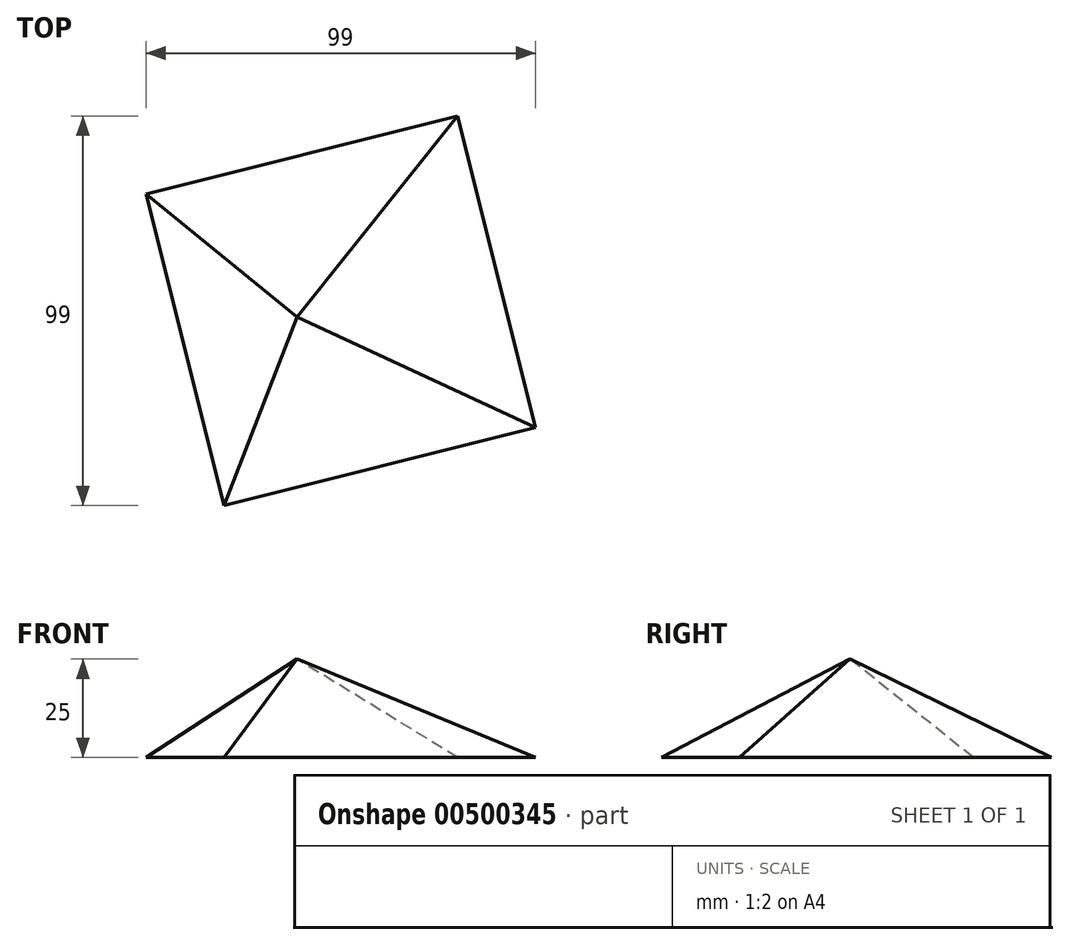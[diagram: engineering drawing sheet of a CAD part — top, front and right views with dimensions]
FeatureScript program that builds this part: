
annotation { "Feature Type Name" : "Feature", "Feature Type Description" : "" }
export const myFeature = defineFeature(function(context is Context, id is Id, definition is map)
    precondition{}
    {
        {
            var Q0;
            Q0=qCreatedBy(makeId("Top.planeOp"),FACE);
            var sketch = newSketch(context, id + "F0", { "sketchPlane" : qUnion([Q0])});
            skCircle(sketch, "E0.cCircle", {"center": v(0, -2.25) * mm, "radius": 57.73 * mm, "construction": true});
            skLineSegment(sketch, "E0.0", {"start": v(-29.7, -51.75) * mm, "end": v(-49.5, 27.45) * mm});
            skLineSegment(sketch, "E0.1", {"start": v(-49.5, 27.45) * mm, "end": v(29.7, 47.25) * mm});
            skLineSegment(sketch, "E0.2", {"start": v(29.7, 47.25) * mm, "end": v(49.5, -31.95) * mm});
            skLineSegment(sketch, "E0.3", {"start": v(49.5, -31.95) * mm, "end": v(-29.7, -51.75) * mm});
            skSolve(sketch);
        }
        {
            var Q0;
            Q0=qCreatedBy(makeId("Top.planeOp"),FACE);
            cPlane(context, id + "F1", {"entities" : qUnion([Q0]), "cplaneType" : CPlaneType.OFFSET, "offset" : 25 * mm, "width" : 150 * mm, "height" : 150 * mm});
        }
        {
            var Q0;
            Q0=qCreatedBy(id+"F1.planeOp",FACE);
            var sketch = newSketch(context, id + "F2", { "sketchPlane" : qUnion([Q0])});
            skPoint(sketch, "E1", {"position": v(-11.1, -3.87) * mm});
            skSolve(sketch);
        }
        {
            var Q0;
            Q0=makeQuery(id+"F0.imprint","IMPRINT",FACE,{"disambiguationData":[TD([[makeQuery(id+"F0.imprint","IMPRINT",EDGE,{"derivedFrom":sQuery(id+"F0.wireOp",EDGE,"E0.0")}),-1.0]])]});
            var Q1;
            Q1=sQuery(id+"F2.wireOp",VERTEX,"E1");
            loft(context, id + "F3", {"sheetProfilesArray" : [{ "sheetProfileEntities" : qUnion([Q0]) }, { "sheetProfileEntities" : qUnion([Q1]) }]});
        }
    });
